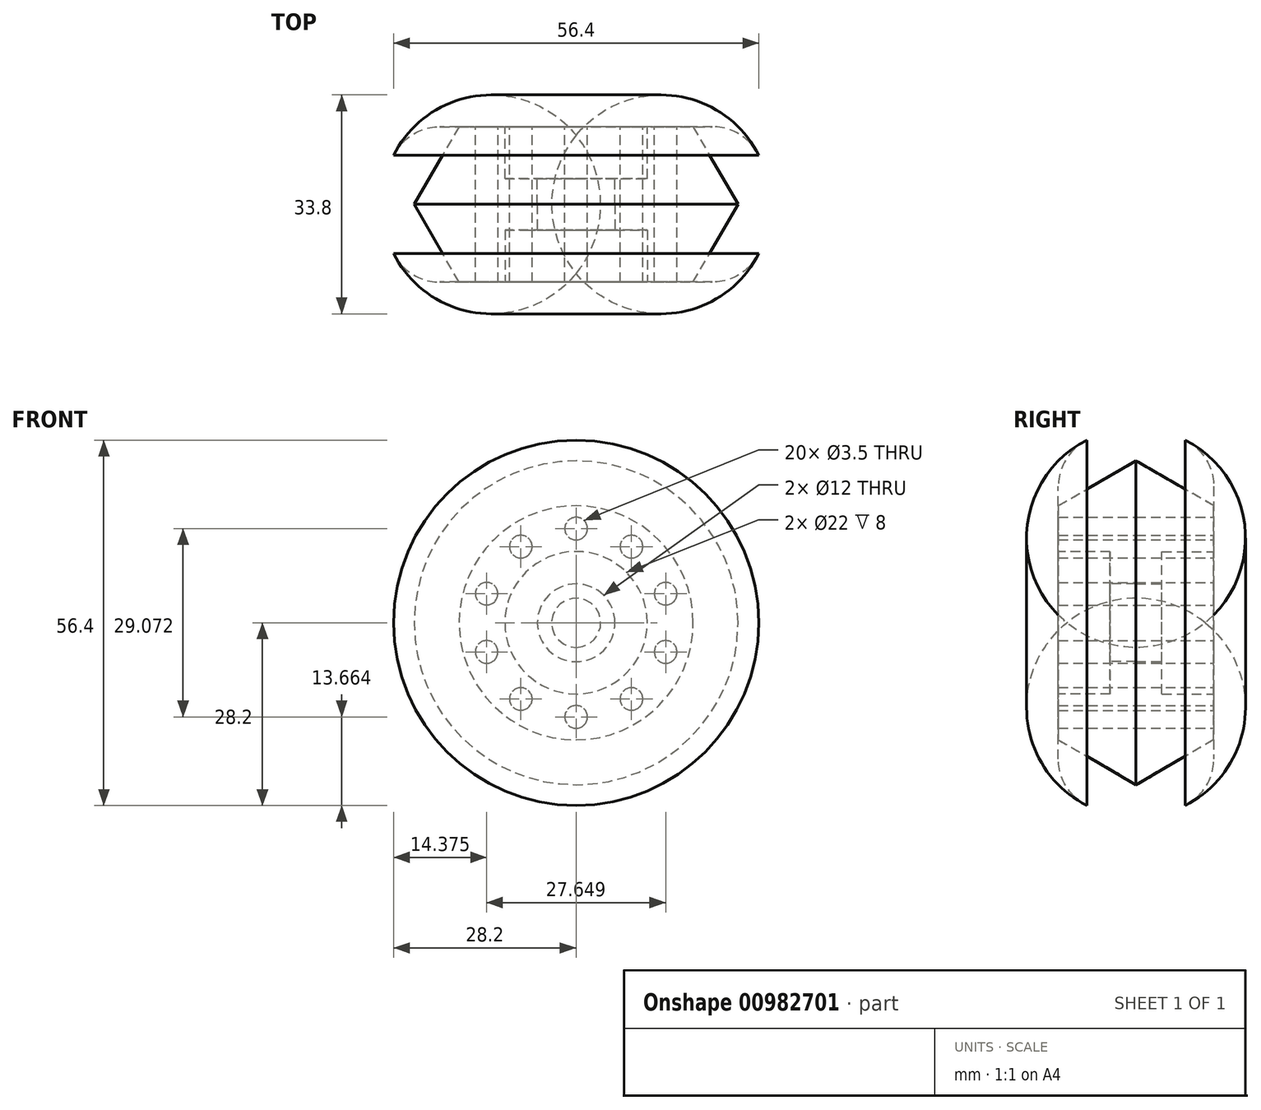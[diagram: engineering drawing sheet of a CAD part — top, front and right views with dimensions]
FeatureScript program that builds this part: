
annotation { "Feature Type Name" : "Feature", "Feature Type Description" : "" }
export const myFeature = defineFeature(function(context is Context, id is Id, definition is map)
    precondition{}
    {
        {
            var Q0;
            Q0=qCreatedBy(makeId("Front.planeOp"),FACE);
            var sketch = newSketch(context, id + "F0", { "sketchPlane" : qUnion([Q0])});
            skCircle(sketch, "E0", {"center": v(0, 0) * mm, "radius": 11 * mm});
            skCircle(sketch, "E1", {"center": v(0, 0) * mm, "radius": 25 * mm});
            skCircle(sketch, "E2", {"center": v(0, 0) * mm, "radius": 6 * mm});
            skCircle(sketch, "E3", {"center": v(0, 0) * mm, "radius": 30 * mm});
            skSolve(sketch);
        }
        {
            var Q0;
            Q0=makeQuery(id+"F0.imprint","IMPRINT",FACE,{"disambiguationData":[TD([[makeQuery(id+"F0.imprint","IMPRINT",EDGE,{"derivedFrom":sQuery(id+"F0.wireOp",EDGE,"E0")}),-1.0]])]});
            var Q1;
            Q1=makeQuery(id+"F0.imprint","IMPRINT",FACE,{"disambiguationData":[TD([[makeQuery(id+"F0.imprint","IMPRINT",EDGE,{"derivedFrom":sQuery(id+"F0.wireOp",EDGE,"E0")}),1.0]])]});
            extrude(context, id + "F1", {"entities" : qUnion([Q0, Q1]), "depth" : 12 * mm, "offsetDistance" : 25 * mm});
        }
        {
            var Q0;
            Q0=makeQuery(id+"F0.imprint","IMPRINT",FACE,{"disambiguationData":[TD([[makeQuery(id+"F0.imprint","IMPRINT",EDGE,{"derivedFrom":sQuery(id+"F0.wireOp",EDGE,"E0")}),1.0]])]});
            extrude(context, id + "F2", {"entities" : qUnion([Q0]), "operationType" : NewBodyOperationType.REMOVE, "depth" : 8 * mm, "offsetDistance" : 25 * mm});
        }
        {
            var Q0;
            Q0=makeQuery(id+"F1.opExtrude","CAP_FACE",FACE,{"disambiguationData":[OSD([sQuery(id+"F0.wireOp",EDGE,"E1"),sQuery(id+"F0.wireOp",EDGE,"E2")])],"isStart":false});
            var sketch = newSketch(context, id + "F3", { "sketchPlane" : qUnion([Q0])});
            skCircle(sketch, "E4", {"center": v(18, 0) * mm, "radius": 2.93 * mm});
            skCircle(sketch, "E5.0", {"center": v(0, 0) * mm, "radius": 11 * mm, "construction": true});
            skCircle(sketch, "E6.0", {"center": v(0, 0) * mm, "radius": 25 * mm, "construction": true});
            skLineSegment(sketch, "E7", {"start": v(11, 0) * mm, "end": v(25, 0) * mm, "construction": true});
            skCircle(sketch, "E8.1.0", {"center": v(0, 18) * mm, "radius": 2.93 * mm});
            skCircle(sketch, "E8.2.0", {"center": v(-18, 0) * mm, "radius": 2.93 * mm});
            skCircle(sketch, "E8.3.0", {"center": v(0, -18) * mm, "radius": 2.93 * mm});
            skLineSegment(sketch, "E9", {"start": v(0, 0) * mm, "end": v(7.78, 7.78) * mm, "construction": true});
            skLineSegment(sketch, "E10", {"start": v(7.78, 7.78) * mm, "end": v(17.68, 17.68) * mm, "construction": true});
            skCircle(sketch, "E11", {"center": v(12.73, 12.73) * mm, "radius": 3.08 * mm});
            skCircle(sketch, "E12.1.0", {"center": v(-12.73, 12.73) * mm, "radius": 3.08 * mm});
            skCircle(sketch, "E12.2.0", {"center": v(-12.73, -12.73) * mm, "radius": 3.08 * mm});
            skCircle(sketch, "E12.3.0", {"center": v(12.73, -12.73) * mm, "radius": 3.08 * mm});
            skSolve(sketch);
        }
        {
            var Q0;
            Q0=qCreatedBy(makeId("Top.planeOp"),FACE);
            var sketch = newSketch(context, id + "F4", { "sketchPlane" : qUnion([Q0])});
            skLineSegment(sketch, "E13", {"start": v(0, 33.2) * mm, "end": v(0, -52.48) * mm, "construction": true});
            skSolve(sketch);
        }
        {
            var Q0;
            Q0=makeQuery(id+"F1.opExtrude","CAP_FACE",FACE,{"disambiguationData":[OSD([sQuery(id+"F0.wireOp",EDGE,"E1"),sQuery(id+"F0.wireOp",EDGE,"E2")])],"isStart":false});
            var sketch = newSketch(context, id + "F5", { "sketchPlane" : qUnion([Q0])});
            skLineSegment(sketch, "E14", {"start": v(-27.1, 0) * mm, "end": v(30.64, 0) * mm});
            skSolve(sketch);
        }
        {
            var Q0;
            Q0=makeQuery(id+"F1.opExtrude","SWEPT_BODY",BODY,{"disambiguationData":[OSD([sQuery(id+"F0.wireOp",EDGE,"E1"),sQuery(id+"F0.wireOp",EDGE,"E2")])]});
            var Q1;
            Q1=sQuery(id+"F5.wireOp",EDGE,"E14");
            transform(context, id + "F6", {"entities" : qUnion([Q0]), "transformType" : TransformType.ROTATION, "transformAxis" : qUnion([Q1]), "angle" : 180 * degree, "makeCopy" : true});
        }
        {
            var Q0;
            Q0=makeQuery(id+"F6.opPattern","COPY",BODY,{"derivedFrom":makeQuery(id+"F1.opExtrude","SWEPT_BODY",BODY,{"disambiguationData":[OSD([sQuery(id+"F0.wireOp",EDGE,"E1"),sQuery(id+"F0.wireOp",EDGE,"E2")])]}),"instanceName":"1"});
            var Q1;
            Q1=sQuery(id+"F4.wireOp",EDGE,"E13");
            transform(context, id + "F7", {"entities" : qUnion([Q0]), "transformType" : TransformType.ROTATION, "transformAxis" : qUnion([Q1]), "angle" : 45 * degree, "makeCopy" : false});
        }
        {
            var Q0;
            Q0=qCreatedBy(makeId("Top.planeOp"),FACE);
            var sketch = newSketch(context, id + "F8", { "sketchPlane" : qUnion([Q0])});
            skLineSegment(sketch, "E15.0", {"start": v(30, 0) * mm, "end": v(-30, 0) * mm, "construction": true});
            skLineSegment(sketch, "E16", {"start": v(-25, -12) * mm, "end": v(-25, 0) * mm, "construction": true});
            skLineSegment(sketch, "E17", {"start": v(-25, -24) * mm, "end": v(-25, -12) * mm, "construction": true});
            skLineSegment(sketch, "E18.0", {"start": v(25, -12) * mm, "end": v(-25, -12) * mm, "construction": true});
            skLineSegment(sketch, "E19", {"start": v(25, 0) * mm, "end": v(25, -12) * mm, "construction": true});
            skLineSegment(sketch, "E20", {"start": v(-25, -12) * mm, "end": v(-18.07, 0) * mm});
            skLineSegment(sketch, "E21.MirrorCS", {"start": v(-25, -12) * mm, "end": v(-18.07, -24) * mm});
            skLineSegment(sketch, "E22", {"start": v(-18.07, 0) * mm, "end": v(-25, 0) * mm});
            skLineSegment(sketch, "E23", {"start": v(-25, -24) * mm, "end": v(-25, 0) * mm});
            skLineSegment(sketch, "E24", {"start": v(-25, -24) * mm, "end": v(-18.07, -24) * mm});
            skSolve(sketch);
        }
        {
            var Q0;
            {var subQ0=sQuery(id+"F8.wireOp",EDGE,"E20");Q0=makeQuery(id+"F8.imprint","IMPRINT",FACE,{"disambiguationData":[TD([[makeQuery(id+"F8.imprint","IMPRINT",EDGE,{"derivedFrom":subQ0}),1.0]])]});}
            var Q1;
            {var subQ0=sQuery(id+"F8.wireOp",EDGE,"E21.MirrorCS");Q1=makeQuery(id+"F8.imprint","IMPRINT",FACE,{"disambiguationData":[TD([[makeQuery(id+"F8.imprint","IMPRINT",EDGE,{"derivedFrom":subQ0}),-1.0]])]});}
            var Q2;
            Q2=sQuery(id+"F4.wireOp",EDGE,"E13");
            revolve(context, id + "F9", {"operationType" : NewBodyOperationType.REMOVE, "surfaceOperationType" : NewSurfaceOperationType.NEW, "entities" : qUnion([Q0, Q1]), "axis" : qUnion([Q2]), "revolveType" : RevolveType.FULL, "oppositeDirection" : true});
        }
        {
            var Q0;
            Q0=qCreatedBy(makeId("Top.planeOp"),FACE);
            var sketch = newSketch(context, id + "F10", { "sketchPlane" : qUnion([Q0])});
            skLineSegment(sketch, "E25.0", {"start": v(30, 0) * mm, "end": v(-30, 0) * mm, "construction": true});
            skLineSegment(sketch, "E26", {"start": v(-25, -12) * mm, "end": v(-18.07, 0) * mm, "construction": true});
            skLineSegment(sketch, "E27.0", {"start": v(-25, -12) * mm, "end": v(-18.07, -24) * mm, "construction": true});
            skLineSegment(sketch, "E28", {"start": v(-30, 0) * mm, "end": v(-30, -12) * mm, "construction": true});
            skPoint(sketch, "E29.0", {"position": v(-25, 0) * mm});
            skPoint(sketch, "E30.0", {"position": v(-25, -24) * mm});
            skLineSegment(sketch, "E31", {"start": v(-18.07, 0) * mm, "end": v(-25, 0) * mm});
            skLineSegment(sketch, "E32", {"start": v(-25, -24) * mm, "end": v(-18.07, -24) * mm});
            skArc(sketch, "E33", {"start": v(-25, 0) * mm, "mid": v(-30, -12) * mm, "end": v(-25, -24) * mm});
            skLineSegment(sketch, "E34", {"start": v(-25, 0) * mm, "end": v(-18.07, 0) * mm});
            skLineSegment(sketch, "E35", {"start": v(-18.07, 0) * mm, "end": v(-25, -12) * mm});
            skLineSegment(sketch, "E36", {"start": v(-25, -12) * mm, "end": v(-18.07, -24) * mm});
            skSolve(sketch);
        }
        {
            var Q0;
            Q0=makeQuery(id+"F10.imprint","IMPRINT",FACE,{"disambiguationData":[TD([[makeQuery(id+"F10.imprint","IMPRINT",EDGE,{"derivedFrom":sQuery(id+"F10.wireOp",EDGE,"E32")}),1.0]])]});
            var Q1;
            Q1=sQuery(id+"F4.wireOp",EDGE,"E13");
            revolve(context, id + "F11", {"surfaceOperationType" : NewSurfaceOperationType.NEW, "entities" : qUnion([Q0]), "axis" : qUnion([Q1]), "revolveType" : RevolveType.FULL});
        }
        {
            var Q0;
            Q0=makeQuery(id+"F1.opExtrude","CAP_FACE",FACE,{"disambiguationData":[OSD([sQuery(id+"F0.wireOp",EDGE,"E1"),sQuery(id+"F0.wireOp",EDGE,"E2")])],"isStart":true});
            var sketch = newSketch(context, id + "F12", { "sketchPlane" : qUnion([Q0])});
            skLineSegment(sketch, "E37", {"start": v(0, -11) * mm, "end": v(0, -18.07) * mm, "construction": true});
            skCircle(sketch, "E38", {"center": v(0, -14.54) * mm, "radius": 1.75 * mm});
            skCircle(sketch, "E39.1.0", {"center": v(8.54, -11.76) * mm, "radius": 1.75 * mm});
            skCircle(sketch, "E39.2.0", {"center": v(13.82, -4.5) * mm, "radius": 1.75 * mm});
            skCircle(sketch, "E39.3.0", {"center": v(13.82, 4.5) * mm, "radius": 1.75 * mm});
            skCircle(sketch, "E39.4.0", {"center": v(8.54, 11.76) * mm, "radius": 1.75 * mm});
            skCircle(sketch, "E39.5.0", {"center": v(0, 14.54) * mm, "radius": 1.75 * mm});
            skCircle(sketch, "E39.6.0", {"center": v(-8.54, 11.76) * mm, "radius": 1.75 * mm});
            skCircle(sketch, "E39.7.0", {"center": v(-13.82, 4.5) * mm, "radius": 1.75 * mm});
            skCircle(sketch, "E39.8.0", {"center": v(-13.82, -4.5) * mm, "radius": 1.75 * mm});
            skCircle(sketch, "E39.9.0", {"center": v(-8.54, -11.76) * mm, "radius": 1.75 * mm});
            skPoint(sketch, "E39.center", {"position": v(0, 0) * mm});
            skSolve(sketch);
        }
        {
            var Q0;
            Q0=qSketchRegion(id+"F12",true);
            extrude(context, id + "F13", {"entities" : qUnion([Q0]), "operationType" : NewBodyOperationType.REMOVE, "endBound" : BoundingType.THROUGH_ALL, "oppositeDirection" : true, "depth" : 25 * mm, "offsetDistance" : 25 * mm});
        }
        {
            var Q0;
            Q0=makeQuery(id+"F11.opRevolve","SWEPT_EDGE",EDGE,{"disambiguationData":[OSD([sQuery(id+"F10.wireOp",EDGE,"E32"),sQuery(id+"F10.wireOp",EDGE,"E33")])]});
            var Q1;
            Q1=makeQuery(id+"F11.opRevolve","SWEPT_EDGE",EDGE,{"disambiguationData":[OSD([sQuery(id+"F10.wireOp",EDGE,"E33"),sQuery(id+"F10.wireOp",EDGE,"E34")])]});
            fillet(context, id + "F14", {"entities" : qUnion([Q0, Q1]), "radius" : 8 * mm, "tangentPropagation" : true, "allowEdgeOverflow" : false});
        }
    });
